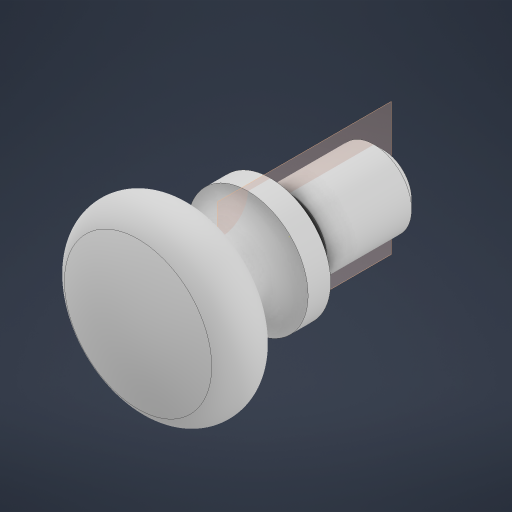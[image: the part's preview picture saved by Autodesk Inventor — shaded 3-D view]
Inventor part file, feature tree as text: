
AUTODESK INVENTOR PART (.ipt)
format: ipt  version: 2024.3 (Build 283343000, 343)  size: 268,800 bytes
history: native  units: mm
features: sketch x5, extrude x2, plane x2, revolve x2, chamfer x1
ambient origin geometry x8: Origin, YZ Plane, XZ Plane, XY Plane, X Axis, Y Axis, Z Axis, Center Point
bodies: Solid1 (feature_tree)
feature tree (12):
  extrude  "Extrusion1"  Depth=5.0mm TaperAngle=0.0deg
  chamfer  "Chamfer1"  Distance=5.0mm Angle=45.0deg
  plane  "Work Plane1"
  sketch  "Sketch2"  dims[d6=10.0mm d7=64.0mm]
  extrude  "Extrusion2"  Depth=10.0mm
  plane  "Work Plane2"
  revolve  "Revolution1"  Angle=90.0deg
  revolve  "Revolution2"  Angle=90.0deg
  sketch  "Sketch1"  dims[d0=40.0mm d1=50.0mm d2=0.0mm d3=5.0mm d4=2.0mm d5=45.0deg]
  sketch  "Sketch3"  dims[d8=12.0mm d9=0.0mm d16=90.0deg]
  sketch  "Sketch5"  dims[d25=32.0mm d27=90.0deg]
  sketch  "Sketch6"
